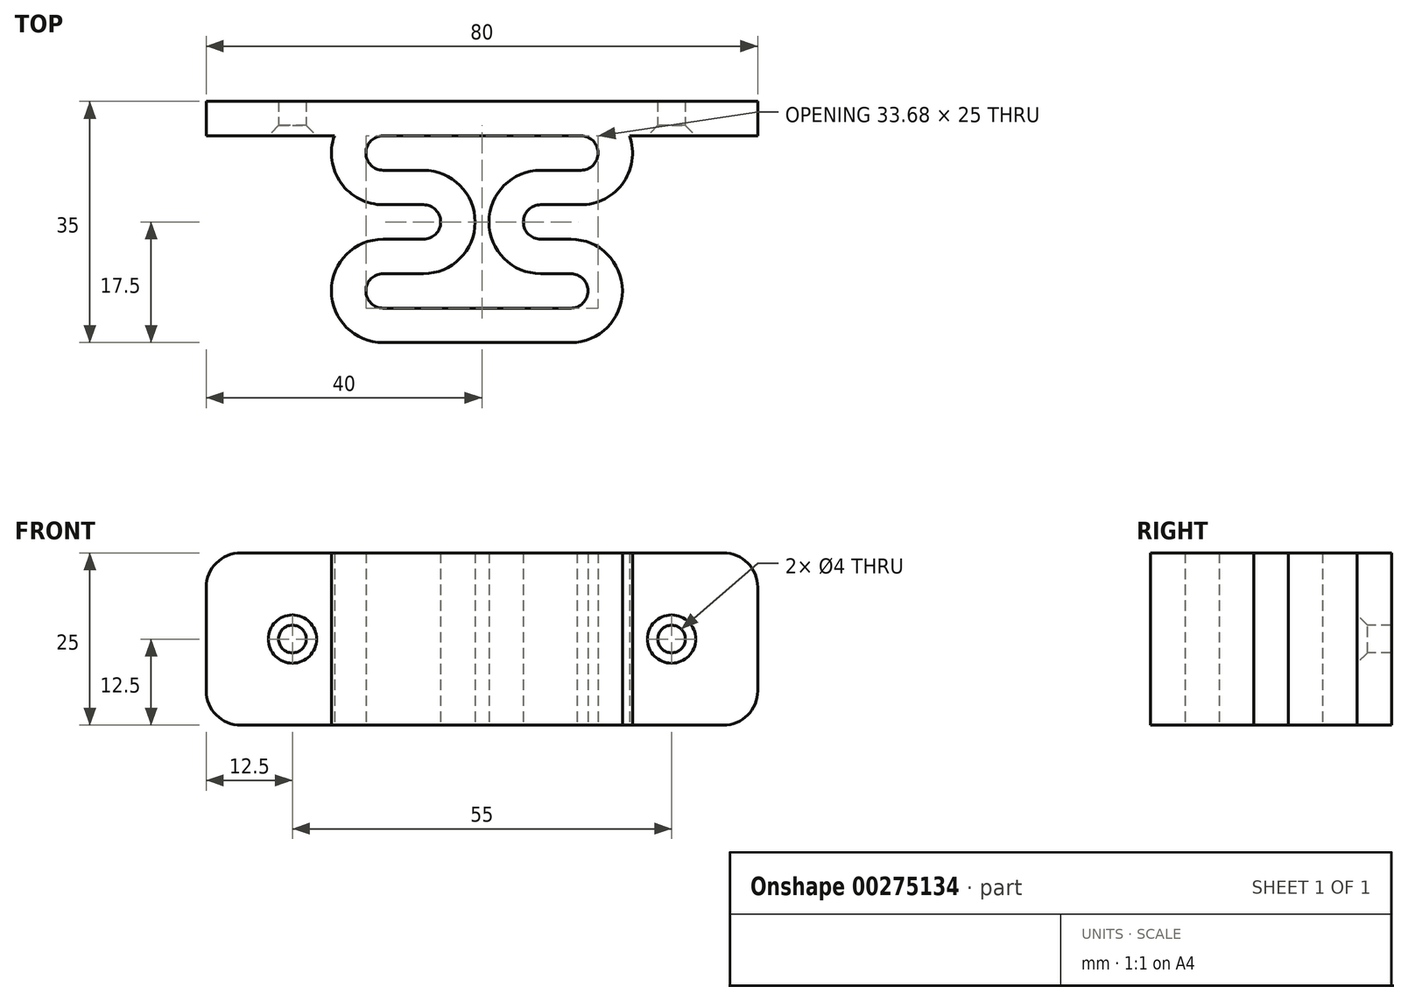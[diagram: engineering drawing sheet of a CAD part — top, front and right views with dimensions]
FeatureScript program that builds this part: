
annotation { "Feature Type Name" : "Feature", "Feature Type Description" : "" }
export const myFeature = defineFeature(function(context is Context, id is Id, definition is map)
    precondition{}
    {
        {
            var Q0;
            Q0=qCreatedBy(makeId("Top.planeOp"),FACE);
            var sketch = newSketch(context, id + "F0", { "sketchPlane" : qUnion([Q0])});
            skCircle(sketch, "E0", {"center": v(-14.34, 10) * mm, "radius": 2.5 * mm});
            skCircle(sketch, "E1", {"center": v(-14.34, 10) * mm, "radius": 7.5 * mm});
            skCircle(sketch, "E2", {"center": v(14.34, 10) * mm, "radius": 7.5 * mm});
            skCircle(sketch, "E3", {"center": v(14.34, 10) * mm, "radius": 2.5 * mm});
            skLineSegment(sketch, "E4", {"start": v(-14.34, 17.5) * mm, "end": v(14.34, 17.5) * mm});
            skPoint(sketch, "E5", {"position": v(0, 17.5) * mm});
            skLineSegment(sketch, "E6", {"start": v(-14.34, 12.5) * mm, "end": v(14.34, 12.5) * mm});
            skCircle(sketch, "E7", {"center": v(-14.34, -10) * mm, "radius": 2.5 * mm});
            skCircle(sketch, "E8", {"center": v(-14.34, -10) * mm, "radius": 7.5 * mm});
            skCircle(sketch, "E9", {"center": v(12.87, -10) * mm, "radius": 2.5 * mm});
            skCircle(sketch, "E10", {"center": v(12.87, -10) * mm, "radius": 7.5 * mm});
            skLineSegment(sketch, "E11", {"start": v(-14.34, -17.5) * mm, "end": v(12.87, -17.5) * mm});
            skLineSegment(sketch, "E12", {"start": v(-14.34, -12.5) * mm, "end": v(12.87, -12.5) * mm});
            skCircle(sketch, "E13", {"center": v(-8.5, 0) * mm, "radius": 2.5 * mm});
            skCircle(sketch, "E14", {"center": v(8.5, 0) * mm, "radius": 2.5 * mm});
            skCircle(sketch, "E15", {"center": v(-8.5, 0) * mm, "radius": 7.5 * mm});
            skCircle(sketch, "E16", {"center": v(8.5, 0) * mm, "radius": 7.5 * mm});
            skLineSegment(sketch, "E17", {"start": v(-14.34, 7.5) * mm, "end": v(-8.5, 7.5) * mm});
            skLineSegment(sketch, "E18", {"start": v(14.34, 7.5) * mm, "end": v(8.5, 7.5) * mm});
            skLineSegment(sketch, "E19", {"start": v(-8.5, 2.5) * mm, "end": v(-14.34, 2.5) * mm});
            skLineSegment(sketch, "E20", {"start": v(8.5, 2.5) * mm, "end": v(13.8, 2.52) * mm});
            skLineSegment(sketch, "E21", {"start": v(-8.5, -2.5) * mm, "end": v(-14.34, -2.5) * mm});
            skLineSegment(sketch, "E22", {"start": v(8.5, -2.5) * mm, "end": v(12.87, -2.5) * mm});
            skLineSegment(sketch, "E23", {"start": v(-14.34, -7.5) * mm, "end": v(-8.5, -7.5) * mm});
            skLineSegment(sketch, "E24", {"start": v(8.5, -7.5) * mm, "end": v(12.87, -7.5) * mm});
            skSolve(sketch);
        }
        {
            var Q0;
            {var subQ0=sQuery(id+"F0.wireOp",EDGE,"E4");Q0=makeQuery(id+"F0.imprint","IMPRINT",FACE,{"disambiguationData":[TD([[makeQuery(id+"F0.imprint","IMPRINT",EDGE,{"derivedFrom":subQ0}),-1.0]])]});}
            var Q1;
            {var subQ0=sQuery(id+"F0.wireOp",EDGE,"E1");var subQ2=sQuery(id+"F0.wireOp",EDGE,"8CR9bk30-KQ4b-ltya-m7mn-kqcPntCiqzbD");var subQ3=makeQuery(id+"F0.imprint","INTERSECT",VERTEX,{"disambiguationData":[OD(0.0)],"derivedFrom":[subQ2,subQ0]});Q1=makeQuery(id+"F0.imprint","IMPRINT",FACE,{"disambiguationData":[TD([[makeQuery(id+"F0.imprint","IMPRINT",EDGE,{"disambiguationData":[TD([[subQ3,1.0]])],"derivedFrom":subQ2}),-1.0]])]});}
            var Q2;
            {var subQ0=sQuery(id+"F0.wireOp",EDGE,"8CR9bk30-KQ4b-ltya-m7mn-kqcPntCiqzbD");var subQ1=makeQuery(id+"F0.imprint","INTERSECT",VERTEX,{"derivedFrom":[subQ0,sQuery(id+"F0.wireOp",EDGE,"E0")]});Q2=makeQuery(id+"F0.imprint","IMPRINT",FACE,{"disambiguationData":[TD([[makeQuery(id+"F0.imprint","IMPRINT",EDGE,{"disambiguationData":[TD([[subQ1,1.0]])],"derivedFrom":subQ0}),1.0]])]});}
            var Q3;
            {var subQ0=sQuery(id+"F0.wireOp",EDGE,"E1");var subQ1=sQuery(id+"F0.wireOp",EDGE,"6h7cOsYY-HjXx-50Em-QmnM-c8Dnv7Tza03D");var subQ2=makeQuery(id+"F0.imprint","INTERSECT",VERTEX,{"derivedFrom":[subQ1,subQ0]});Q3=makeQuery(id+"F0.imprint","IMPRINT",FACE,{"disambiguationData":[TD([[makeQuery(id+"F0.imprint","IMPRINT",EDGE,{"disambiguationData":[TD([[subQ2,1.0]])],"derivedFrom":subQ1}),-1.0]])]});}
            var Q4;
            {var subQ0=sQuery(id+"F0.wireOp",EDGE,"E8");var subQ1=sQuery(id+"F0.wireOp",EDGE,"8CR9bk30-KQ4b-ltya-m7mn-kqcPntCiqzbD");var subQ2=makeQuery(id+"F0.imprint","INTERSECT",VERTEX,{"disambiguationData":[OD(0.0)],"derivedFrom":[subQ1,subQ0]});Q4=makeQuery(id+"F0.imprint","IMPRINT",FACE,{"disambiguationData":[TD([[makeQuery(id+"F0.imprint","IMPRINT",EDGE,{"disambiguationData":[TD([[subQ2,-1.0]])],"derivedFrom":subQ1}),1.0]])]});}
            var Q5;
            {var subQ0=sQuery(id+"F0.wireOp",EDGE,"E8");var subQ4=sQuery(id+"F0.wireOp",EDGE,"8CR9bk30-KQ4b-ltya-m7mn-kqcPntCiqzbD");var subQ5=makeQuery(id+"F0.imprint","INTERSECT",VERTEX,{"disambiguationData":[OD(0.0)],"derivedFrom":[subQ4,subQ0]});Q5=makeQuery(id+"F0.imprint","IMPRINT",FACE,{"disambiguationData":[TD([[makeQuery(id+"F0.imprint","IMPRINT",EDGE,{"disambiguationData":[TD([[subQ5,-1.0]])],"derivedFrom":subQ4}),-1.0]])]});}
            var Q6;
            {var subQ0=sQuery(id+"F0.wireOp",EDGE,"E11");Q6=makeQuery(id+"F0.imprint","IMPRINT",FACE,{"disambiguationData":[TD([[makeQuery(id+"F0.imprint","IMPRINT",EDGE,{"derivedFrom":subQ0}),1.0]])]});}
            var Q7;
            {var subQ0=sQuery(id+"F0.wireOp",EDGE,"E10");var subQ2=sQuery(id+"F0.wireOp",EDGE,"DIOqt0p8-QBxR-8iWn-KdwK-cJBDFyHMyHgb");var subQ3=makeQuery(id+"F0.imprint","INTERSECT",VERTEX,{"disambiguationData":[OD(0.0)],"derivedFrom":[subQ2,subQ0]});Q7=makeQuery(id+"F0.imprint","IMPRINT",FACE,{"disambiguationData":[TD([[makeQuery(id+"F0.imprint","IMPRINT",EDGE,{"disambiguationData":[TD([[subQ3,1.0]])],"derivedFrom":subQ2}),-1.0]])]});}
            var Q8;
            {var subQ0=sQuery(id+"F0.wireOp",EDGE,"E10");var subQ1=sQuery(id+"F0.wireOp",EDGE,"DIOqt0p8-QBxR-8iWn-KdwK-cJBDFyHMyHgb");var subQ2=makeQuery(id+"F0.imprint","INTERSECT",VERTEX,{"disambiguationData":[OD(1.0)],"derivedFrom":[subQ1,subQ0]});Q8=makeQuery(id+"F0.imprint","IMPRINT",FACE,{"disambiguationData":[TD([[makeQuery(id+"F0.imprint","IMPRINT",EDGE,{"disambiguationData":[TD([[subQ2,-1.0]])],"derivedFrom":subQ1}),1.0]])]});}
            var Q9;
            {var subQ0=sQuery(id+"F0.wireOp",EDGE,"DIOqt0p8-QBxR-8iWn-KdwK-cJBDFyHMyHgb");var subQ1=sQuery(id+"F0.wireOp",EDGE,"E2");var subQ2=makeQuery(id+"F0.imprint","INTERSECT",VERTEX,{"disambiguationData":[OD(1.0)],"derivedFrom":[subQ1,subQ0]});Q9=makeQuery(id+"F0.imprint","IMPRINT",FACE,{"disambiguationData":[TD([[makeQuery(id+"F0.imprint","IMPRINT",EDGE,{"disambiguationData":[TD([[subQ2,-1.0]])],"derivedFrom":subQ1}),-1.0]])]});}
            var Q10;
            {var subQ1=sQuery(id+"F0.wireOp",EDGE,"E2");var subQ7=makeQuery(id+"F0.imprint","INTERSECT",VERTEX,{"derivedFrom":[subQ1,sQuery(id+"F0.wireOp",EDGE,"E4")]});Q10=makeQuery(id+"F0.imprint","IMPRINT",FACE,{"disambiguationData":[TD([[makeQuery(id+"F0.imprint","IMPRINT",EDGE,{"disambiguationData":[TD([[subQ7,-1.0]])],"derivedFrom":subQ1}),1.0]])]});}
            var Q11;
            {var subQ0=sQuery(id+"F0.wireOp",EDGE,"DIOqt0p8-QBxR-8iWn-KdwK-cJBDFyHMyHgb");var subQ1=sQuery(id+"F0.wireOp",EDGE,"E2");var subQ2=makeQuery(id+"F0.imprint","INTERSECT",VERTEX,{"disambiguationData":[OD(1.0)],"derivedFrom":[subQ1,subQ0]});Q11=makeQuery(id+"F0.imprint","IMPRINT",FACE,{"disambiguationData":[TD([[makeQuery(id+"F0.imprint","IMPRINT",EDGE,{"disambiguationData":[TD([[subQ2,-1.0]])],"derivedFrom":subQ1}),1.0]])]});}
            var Q12;
            {var subQ8=sQuery(id+"F0.wireOp",EDGE,"E17");Q12=makeQuery(id+"F0.imprint","IMPRINT",FACE,{"disambiguationData":[TD([[makeQuery(id+"F0.imprint","IMPRINT",EDGE,{"derivedFrom":subQ8}),-1.0]])]});}
            var Q13;
            {var subQ0=sQuery(id+"F0.wireOp",EDGE,"E1");var subQ1=makeQuery(id+"F0.imprint","INTERSECT",VERTEX,{"derivedFrom":[subQ0,sQuery(id+"F0.wireOp",EDGE,"E19")]});Q13=makeQuery(id+"F0.imprint","IMPRINT",FACE,{"disambiguationData":[TD([[makeQuery(id+"F0.imprint","IMPRINT",EDGE,{"disambiguationData":[TD([[subQ1,1.0]])],"derivedFrom":subQ0}),1.0]])]});}
            var Q14;
            {var subQ5=sQuery(id+"F0.wireOp",EDGE,"E19");Q14=makeQuery(id+"F0.imprint","IMPRINT",FACE,{"disambiguationData":[TD([[makeQuery(id+"F0.imprint","IMPRINT",EDGE,{"derivedFrom":subQ5}),-1.0]])]});}
            var Q15;
            {var subQ0=sQuery(id+"F0.wireOp",EDGE,"E8");var subQ1=makeQuery(id+"F0.imprint","INTERSECT",VERTEX,{"derivedFrom":[subQ0,sQuery(id+"F0.wireOp",EDGE,"E21")]});Q15=makeQuery(id+"F0.imprint","IMPRINT",FACE,{"disambiguationData":[TD([[makeQuery(id+"F0.imprint","IMPRINT",EDGE,{"disambiguationData":[TD([[subQ1,1.0]])],"derivedFrom":subQ0}),1.0]])]});}
            var Q16;
            {var subQ0=sQuery(id+"F0.wireOp",EDGE,"E10");var subQ1=makeQuery(id+"F0.imprint","INTERSECT",VERTEX,{"derivedFrom":[subQ0,sQuery(id+"F0.wireOp",EDGE,"E22")]});Q16=makeQuery(id+"F0.imprint","IMPRINT",FACE,{"disambiguationData":[TD([[makeQuery(id+"F0.imprint","IMPRINT",EDGE,{"disambiguationData":[TD([[subQ1,1.0]])],"derivedFrom":subQ0}),1.0]])]});}
            var Q17;
            {var subQ0=sQuery(id+"F0.wireOp",EDGE,"E2");var subQ1=makeQuery(id+"F0.imprint","INTERSECT",VERTEX,{"derivedFrom":[subQ0,sQuery(id+"F0.wireOp",EDGE,"E20")]});Q17=makeQuery(id+"F0.imprint","IMPRINT",FACE,{"disambiguationData":[TD([[makeQuery(id+"F0.imprint","IMPRINT",EDGE,{"disambiguationData":[TD([[subQ1,1.0]])],"derivedFrom":subQ0}),1.0]])]});}
            var Q18;
            {var subQ5=sQuery(id+"F0.wireOp",EDGE,"E20");Q18=makeQuery(id+"F0.imprint","IMPRINT",FACE,{"disambiguationData":[TD([[makeQuery(id+"F0.imprint","IMPRINT",EDGE,{"derivedFrom":subQ5}),1.0]])]});}
            var Q19;
            {var subQ8=sQuery(id+"F0.wireOp",EDGE,"E23");Q19=makeQuery(id+"F0.imprint","IMPRINT",FACE,{"disambiguationData":[TD([[makeQuery(id+"F0.imprint","IMPRINT",EDGE,{"derivedFrom":subQ8}),1.0]])]});}
            var Q20;
            {var subQ8=sQuery(id+"F0.wireOp",EDGE,"E24");Q20=makeQuery(id+"F0.imprint","IMPRINT",FACE,{"disambiguationData":[TD([[makeQuery(id+"F0.imprint","IMPRINT",EDGE,{"derivedFrom":subQ8}),1.0]])]});}
            extrude(context, id + "F1", {"entities" : qUnion([Q0, Q1, Q2, Q3, Q4, Q5, Q6, Q7, Q8, Q9, Q10, Q11, Q12, Q13, Q14, Q15, Q16, Q17, Q18, Q19, Q20]), "depth" : 25 * mm});
        }
        {
            var Q0;
            Q0=qCreatedBy(makeId("Right.planeOp"),FACE);
            var sketch = newSketch(context, id + "F2", { "sketchPlane" : qUnion([Q0])});
            skLineSegment(sketch, "E25.bottom", {"start": v(17.5, 25) * mm, "end": v(12.5, 25) * mm});
            skLineSegment(sketch, "E25.top", {"start": v(17.5, 0) * mm, "end": v(12.5, 0) * mm});
            skLineSegment(sketch, "E25.left", {"start": v(17.5, 25) * mm, "end": v(17.5, 0) * mm});
            skLineSegment(sketch, "E25.right", {"start": v(12.5, 25) * mm, "end": v(12.5, 0) * mm});
            skSolve(sketch);
        }
        {
            var Q0;
            Q0=qSketchRegion(id+"F2",true);
            extrude(context, id + "F3", {"entities" : qUnion([Q0]), "operationType" : NewBodyOperationType.ADD, "endBound" : BoundingType.SYMMETRIC, "depth" : 80 * mm});
        }
        {
            var Q0;
            Q0=makeQuery(id+"F3.opExtrude","CAP_EDGE",EDGE,{"disambiguationData":[OSD([sQuery(id+"F2.wireOp",EDGE,"E25.top")])],"isStart":false});
            var Q1;
            Q1=makeQuery(id+"F3.opExtrude","CAP_EDGE",EDGE,{"disambiguationData":[OSD([sQuery(id+"F2.wireOp",EDGE,"E25.bottom")])],"isStart":false});
            var Q2;
            Q2=makeQuery(id+"F3.opExtrude","CAP_EDGE",EDGE,{"disambiguationData":[OSD([sQuery(id+"F2.wireOp",EDGE,"E25.bottom")])],"isStart":true});
            var Q3;
            Q3=makeQuery(id+"F3.opExtrude","CAP_EDGE",EDGE,{"disambiguationData":[OSD([sQuery(id+"F2.wireOp",EDGE,"E25.top")])],"isStart":true});
            fillet(context, id + "F4", {"entities" : qUnion([Q0, Q1, Q2, Q3]), "radius" : 5 * mm, "tangentPropagation" : true, "allowEdgeOverflow" : false});
        }
        {
            var Q0;
            {var subQ0=sQuery(id+"F0.wireOp",EDGE,"E1");var subQ25=sQuery(id+"F2.wireOp",EDGE,"E25.right");Q0=makeQuery(id+"F3.boolean.opBoolean","SPLIT",FACE,{"disambiguationData":[TD([makeQuery(id+"F1.opExtrude","SWEPT_FACE",FACE,{"disambiguationData":[OSD([subQ0])]})])],"derivedFrom":makeQuery(id+"F3.opExtrude","SWEPT_FACE",FACE,{"disambiguationData":[OSD([subQ25])]})});}
            var sketch = newSketch(context, id + "F5", { "sketchPlane" : qUnion([Q0])});
            skPoint(sketch, "E26", {"position": v(-27.5, 12.5) * mm});
            skPoint(sketch, "E27", {"position": v(27.5, 12.5) * mm});
            skPoint(sketch, "E28", {"position": v(-40, 12.5) * mm});
            skLineSegment(sketch, "E29", {"start": v(-40, 12.5) * mm, "end": v(-27.5, 12.5) * mm});
            skLineSegment(sketch, "E30", {"start": v(-27.5, 25) * mm, "end": v(-27.5, 12.5) * mm});
            skLineSegment(sketch, "E31", {"start": v(40, 12.5) * mm, "end": v(27.5, 12.5) * mm});
            skLineSegment(sketch, "E32", {"start": v(27.5, 12.5) * mm, "end": v(27.5, 25) * mm});
            skSolve(sketch);
        }
        {
            var Q0;
            Q0=sQuery(id+"F5.wireOp",VERTEX,"E27");
            var Q1;
            Q1=sQuery(id+"F5.wireOp",VERTEX,"E26");
            var Q2;
            Q2=makeQuery(id+"F1.opExtrude","SWEPT_BODY",BODY,{"disambiguationData":[OSD([sQuery(id+"F0.wireOp",EDGE,"E0"),sQuery(id+"F0.wireOp",EDGE,"E1"),sQuery(id+"F0.wireOp",EDGE,"E2"),sQuery(id+"F0.wireOp",EDGE,"E3"),sQuery(id+"F0.wireOp",EDGE,"E4"),sQuery(id+"F0.wireOp",EDGE,"E6"),sQuery(id+"F0.wireOp",EDGE,"E7"),sQuery(id+"F0.wireOp",EDGE,"E8"),sQuery(id+"F0.wireOp",EDGE,"E9"),sQuery(id+"F0.wireOp",EDGE,"E10"),sQuery(id+"F0.wireOp",EDGE,"E11"),sQuery(id+"F0.wireOp",EDGE,"E12"),sQuery(id+"F0.wireOp",EDGE,"E13"),sQuery(id+"F0.wireOp",EDGE,"E14"),sQuery(id+"F0.wireOp",EDGE,"E15"),sQuery(id+"F0.wireOp",EDGE,"E16"),sQuery(id+"F0.wireOp",EDGE,"E17"),sQuery(id+"F0.wireOp",EDGE,"E18"),sQuery(id+"F0.wireOp",EDGE,"E19"),sQuery(id+"F0.wireOp",EDGE,"E20"),sQuery(id+"F0.wireOp",EDGE,"E21"),sQuery(id+"F0.wireOp",EDGE,"E22"),sQuery(id+"F0.wireOp",EDGE,"E23"),sQuery(id+"F0.wireOp",EDGE,"E24")])]});
            hole(context, id + "F6", {"style" : HoleStyle.C_SINK, "endStyle" : HoleEndStyle.THROUGH, "holeDiameter" : 4 * mm, "cSinkDiameter" : 7 * mm, "cSinkAngle" : 90 * degree, "tappedDepth" : 13.2 * mm, "tapClearance" : 3, "startFromSketch" : true, "locations" : qUnion([Q0, Q1]), "scope" : qUnion([Q2])});
        }
    });
